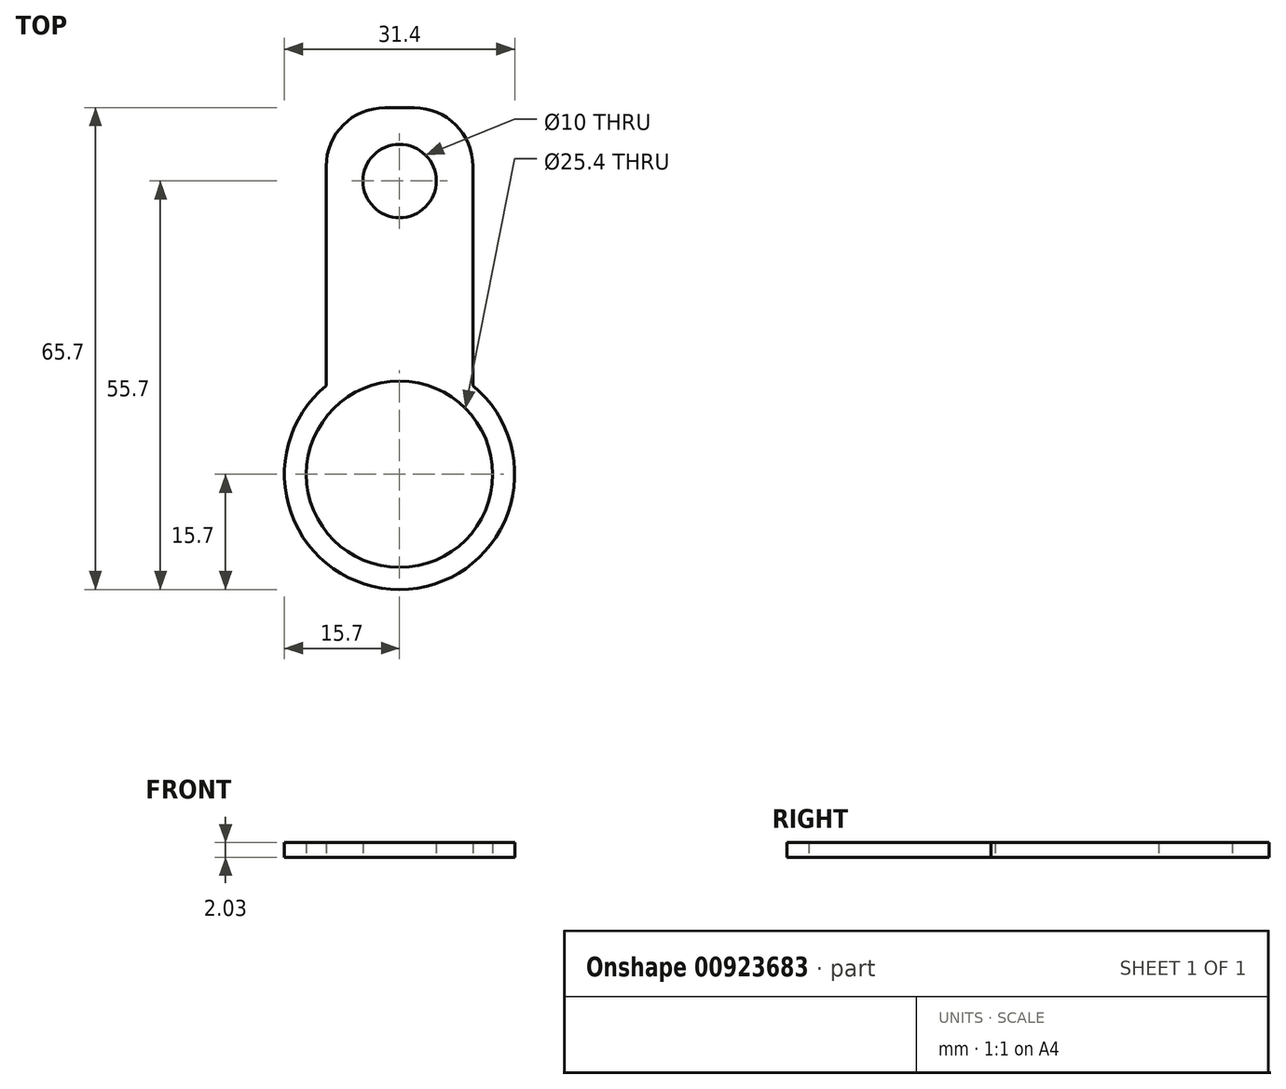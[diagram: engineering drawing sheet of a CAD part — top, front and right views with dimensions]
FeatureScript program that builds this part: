
annotation { "Feature Type Name" : "Feature", "Feature Type Description" : "" }
export const myFeature = defineFeature(function(context is Context, id is Id, definition is map)
    precondition{}
    {
        {
            var Q0;
            Q0=qCreatedBy(makeId("Top.planeOp"),FACE);
            var sketch = newSketch(context, id + "F0", { "sketchPlane" : qUnion([Q0])});
            skLineSegment(sketch, "E0.top", {"start": v(-2, 50) * mm, "end": v(2, 50) * mm});
            skLineSegment(sketch, "E0.left", {"start": v(-10, 12.1) * mm, "end": v(-10, 42) * mm});
            skLineSegment(sketch, "E0.right", {"start": v(10, 12.1) * mm, "end": v(10, 42) * mm});
            skCircle(sketch, "E1", {"center": v(0, 40) * mm, "radius": 5 * mm});
            skLineSegment(sketch, "E2", {"start": v(5, 40) * mm, "end": v(10, 40) * mm, "construction": true});
            skLineSegment(sketch, "E3", {"start": v(0, 45) * mm, "end": v(0, 50) * mm, "construction": true});
            skPoint(sketch, "E4.visualSharp", {"position": v(-10, 50) * mm});
            skArc(sketch, "E4.filletArc", {"start": v(-2, 50) * mm, "mid": v(-7.66, 47.66) * mm, "end": v(-10, 42) * mm});
            skPoint(sketch, "E5.visualSharp", {"position": v(10, 50) * mm});
            skArc(sketch, "E5.filletArc", {"start": v(10, 42) * mm, "mid": v(7.66, 47.66) * mm, "end": v(2, 50) * mm});
            skCircle(sketch, "E6", {"center": v(0, 0) * mm, "radius": 12.7 * mm});
            skArc(sketch, "E7", {"start": v(-10, 12.1) * mm, "mid": v(0, -15.7) * mm, "end": v(10, 12.1) * mm});
            skLineSegment(sketch, "E8", {"start": v(12.7, 0) * mm, "end": v(15.7, 0) * mm, "construction": true});
            skSolve(sketch);
        }
        {
            var Q0;
            Q0=qSketchRegion(id+"F0",true);
            extrude(context, id + "F1", {"entities" : qUnion([Q0]), "depth" : 2.03 * mm, "offsetDistance" : 25 * mm});
        }
    });
